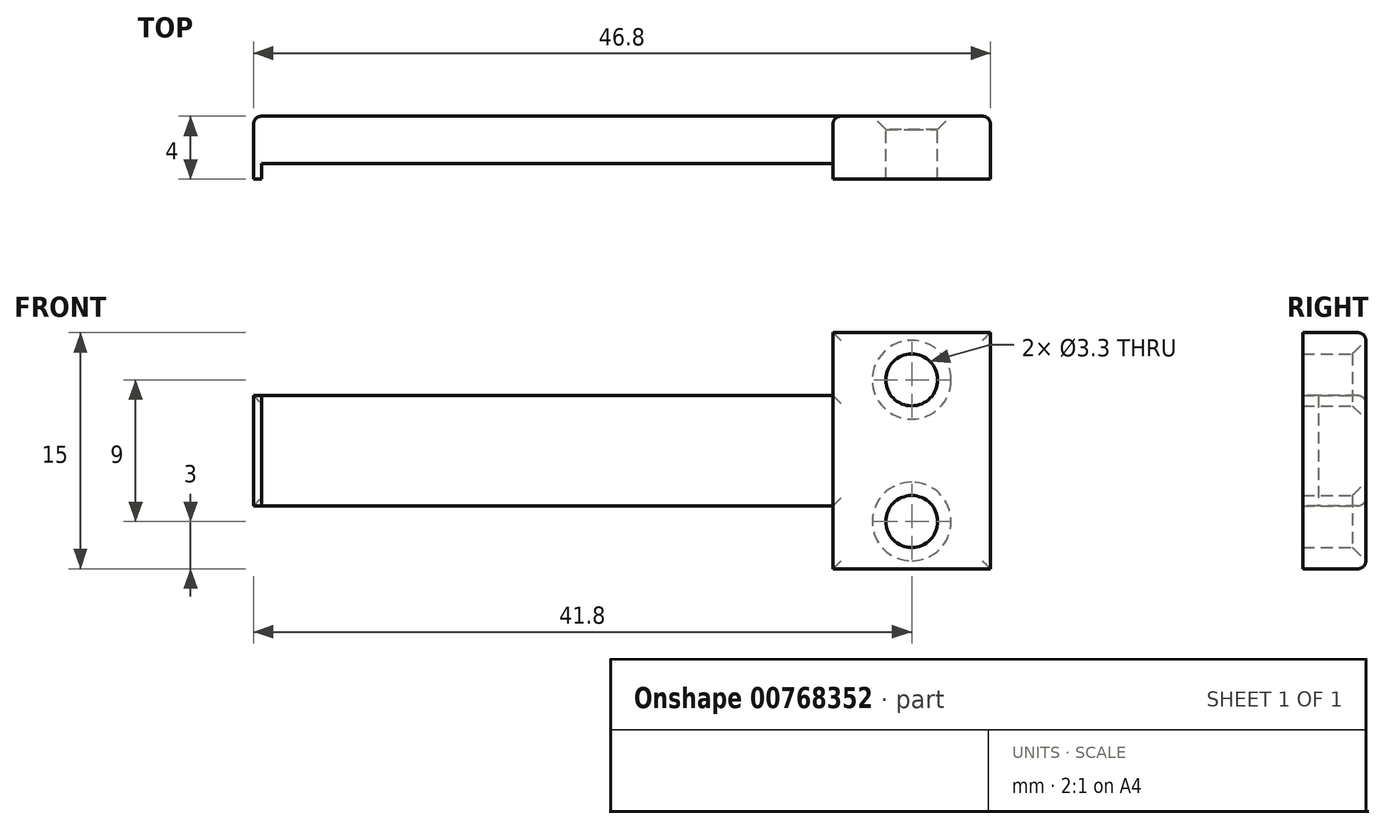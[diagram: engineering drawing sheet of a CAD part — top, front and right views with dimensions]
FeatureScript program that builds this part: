
annotation { "Feature Type Name" : "Feature", "Feature Type Description" : "" }
export const myFeature = defineFeature(function(context is Context, id is Id, definition is map)
    precondition{}
    {
        {
            assignVariable(context, id + "F0", {"name" : "clipwidht", "anyValue" : 7});
        }
        {
            assignVariable(context, id + "F1", {"name" : "footwidht", "anyValue" : 4});
        }
        {
            var Q0;
            Q0=qCreatedBy(makeId("Top.planeOp"),FACE);
            var sketch = newSketch(context, id + "F2", { "sketchPlane" : qUnion([Q0])});
            skLineSegment(sketch, "E0", {"start": v(0, 0) * mm, "end": v(0, 4) * mm});
            skLineSegment(sketch, "E1", {"start": v(0, 4) * mm, "end": v(46.8, 4) * mm});
            skLineSegment(sketch, "E2", {"start": v(46.8, 4) * mm, "end": v(46.8, 0) * mm});
            skLineSegment(sketch, "E3", {"start": v(46.8, 0) * mm, "end": v(36.8, 0) * mm});
            skLineSegment(sketch, "E4", {"start": v(36.8, 0) * mm, "end": v(36.8, 1) * mm});
            skLineSegment(sketch, "E5", {"start": v(36.8, 1) * mm, "end": v(0.5, 1) * mm});
            skLineSegment(sketch, "E6", {"start": v(0.5, 1) * mm, "end": v(0.5, 0) * mm});
            skLineSegment(sketch, "E7", {"start": v(0.5, 0) * mm, "end": v(0, 0) * mm});
            skSolve(sketch);
        }
        {
            var Q0;
            Q0=makeQuery(id+"F2.imprint","IMPRINT",FACE,{"disambiguationData":[TD([[makeQuery(id+"F2.imprint","IMPRINT",EDGE,{"derivedFrom":sQuery(id+"F2.wireOp",EDGE,"E0")}),-1.0]])]});
            extrude(context, id + "F3", {"entities" : qUnion([Q0]), "depth" : (getVariable(context, 'clipwidht')) * mm, "offsetDistance" : 25 * mm});
        }
        {
            var Q0;
            Q0=makeQuery(id+"F3.opExtrude","CAP_FACE",FACE,{"disambiguationData":[OSD([sQuery(id+"F2.wireOp",EDGE,"E0"),sQuery(id+"F2.wireOp",EDGE,"E1"),sQuery(id+"F2.wireOp",EDGE,"E2"),sQuery(id+"F2.wireOp",EDGE,"E3"),sQuery(id+"F2.wireOp",EDGE,"E4"),sQuery(id+"F2.wireOp",EDGE,"E5"),sQuery(id+"F2.wireOp",EDGE,"E6"),sQuery(id+"F2.wireOp",EDGE,"E7")])],"isStart":false});
            var sketch = newSketch(context, id + "F4", { "sketchPlane" : qUnion([Q0])});
            skLineSegment(sketch, "E8.bottom", {"start": v(36.8, 0) * mm, "end": v(46.8, 0) * mm});
            skLineSegment(sketch, "E8.top", {"start": v(36.8, 4) * mm, "end": v(46.8, 4) * mm});
            skLineSegment(sketch, "E8.left", {"start": v(36.8, 0) * mm, "end": v(36.8, 4) * mm});
            skLineSegment(sketch, "E8.right", {"start": v(46.8, 0) * mm, "end": v(46.8, 4) * mm});
            skLineSegment(sketch, "E9", {"start": v(41.8, 4) * mm, "end": v(41.8, 0) * mm, "construction": true});
            skSolve(sketch);
        }
        {
            var Q0;
            {var subQ3=sQuery(id+"F4.wireOp",EDGE,"E8.bottom");Q0=makeQuery(id+"F4.imprint","IMPRINT",FACE,{"disambiguationData":[TD([[makeQuery(id+"F4.imprint","IMPRINT",EDGE,{"derivedFrom":subQ3}),-1.0]])]});}
            extrude(context, id + "F5", {"entities" : qUnion([Q0]), "operationType" : NewBodyOperationType.ADD, "depth" : getVariable(context, 'footwidht') * mm, "offsetDistance" : 25 * mm, "hasSecondDirection" : true, "secondDirectionOppositeDirection" : true, "secondDirectionDepth" : (getVariable(context, 'footwidht') + getVariable(context, 'clipwidht')) * mm});
        }
        {
            var Q0;
            Q0=makeQuery(id+"F5.boolean.opBoolean","MERGE",FACE,{"derivedFrom":[makeQuery(id+"F3.opExtrude","SWEPT_FACE",FACE,{"disambiguationData":[OSD([sQuery(id+"F2.wireOp",EDGE,"E1")])]}),makeQuery(id+"F5.opExtrude","SWEPT_FACE",FACE,{"disambiguationData":[OSD([sQuery(id+"F4.wireOp",EDGE,"E8.top")])]})]});
            var sketch = newSketch(context, id + "F6", { "sketchPlane" : qUnion([Q0])});
            skLineSegment(sketch, "E10", {"start": v(-41.8, 11) * mm, "end": v(-41.8, -4) * mm, "construction": true});
            skLineSegment(sketch, "E11", {"start": v(-36.8, 9) * mm, "end": v(-46.8, 9) * mm, "construction": true});
            skLineSegment(sketch, "E12", {"start": v(-36.8, -2) * mm, "end": v(-46.8, -2) * mm, "construction": true});
            skPoint(sketch, "E13", {"position": v(-41.8, 9) * mm});
            skPoint(sketch, "E14", {"position": v(-41.8, -2) * mm});
            skPoint(sketch, "E15", {"position": v(-41.8, 8) * mm});
            skPoint(sketch, "E16", {"position": v(-41.8, -1) * mm});
            skLineSegment(sketch, "E17", {"start": v(-46.8, 3.5) * mm, "end": v(0, 3.5) * mm, "construction": true});
            skSolve(sketch);
        }
        {
            var Q0;
            Q0=sQuery(id+"F6.wireOp",VERTEX,"E15");
            var Q1;
            Q1=sQuery(id+"F6.wireOp",VERTEX,"E16");
            var Q2;
            Q2=makeQuery(id+"F3.opExtrude","SWEPT_BODY",BODY,{"disambiguationData":[OSD([sQuery(id+"F2.wireOp",EDGE,"E0"),sQuery(id+"F2.wireOp",EDGE,"E1"),sQuery(id+"F2.wireOp",EDGE,"E2"),sQuery(id+"F2.wireOp",EDGE,"E3"),sQuery(id+"F2.wireOp",EDGE,"E4"),sQuery(id+"F2.wireOp",EDGE,"E5"),sQuery(id+"F2.wireOp",EDGE,"E6"),sQuery(id+"F2.wireOp",EDGE,"E7")])]});
            hole(context, id + "F7", {"style" : HoleStyle.C_SINK, "endStyle" : HoleEndStyle.THROUGH, "holeDiameter" : 3.3 * mm, "cSinkDiameter" : 5 * mm, "cSinkAngle" : 90 * degree, "majorDiameter" : 5 * mm, "isTappedThrough" : true, "tappedDepth" : 12 * mm, "tapClearance" : 3, "startFromSketch" : true, "locations" : qUnion([Q0, Q1]), "scope" : qUnion([Q2])});
        }
        {
            var Q0;
            Q0=makeQuery(id+"F3.opExtrude","CAP_EDGE",EDGE,{"disambiguationData":[OSD([sQuery(id+"F2.wireOp",EDGE,"E1")])],"isStart":false});
            var Q1;
            Q1=makeQuery(id+"F3.opExtrude","SWEPT_EDGE",EDGE,{"disambiguationData":[OSD([sQuery(id+"F2.wireOp",EDGE,"E0"),sQuery(id+"F2.wireOp",EDGE,"E1")])]});
            var Q2;
            Q2=makeQuery(id+"F3.opExtrude","CAP_EDGE",EDGE,{"disambiguationData":[OSD([sQuery(id+"F2.wireOp",EDGE,"E1")])],"isStart":true});
            var Q3;
            Q3=makeQuery(id+"F5.opExtrude","CAP_EDGE",EDGE,{"disambiguationData":[OSD([sQuery(id+"F4.wireOp",EDGE,"E8.top")])],"isStart":true});
            var Q4;
            {var subQ0=sQuery(id+"F4.wireOp",EDGE,"E8.left");var subQ1=sQuery(id+"F4.wireOp",EDGE,"E8.top");var subQ2=sQuery(id+"F2.wireOp",EDGE,"E1");Q4=makeQuery(id+"F5.boolean.opBoolean","SPLIT",EDGE,{"disambiguationData":[TD([makeQuery(id+"F5.opExtrude","CAP_FACE",FACE,{"disambiguationData":[OSD([sQuery(id+"F4.wireOp",EDGE,"E8.bottom"),subQ1,subQ0,sQuery(id+"F4.wireOp",EDGE,"E8.right")])],"isStart":true})])],"derivedFrom":makeQuery(id+"F5.opExtrude","SWEPT_EDGE",EDGE,{"disambiguationData":[OSD([subQ2,subQ1,subQ0])]})});}
            var Q5;
            {var subQ0=sQuery(id+"F4.wireOp",EDGE,"E8.left");var subQ1=sQuery(id+"F4.wireOp",EDGE,"E8.top");var subQ2=sQuery(id+"F2.wireOp",EDGE,"E1");Q5=makeQuery(id+"F5.boolean.opBoolean","SPLIT",EDGE,{"disambiguationData":[TD([makeQuery(id+"F5.opExtrude","CAP_FACE",FACE,{"disambiguationData":[OSD([sQuery(id+"F4.wireOp",EDGE,"E8.bottom"),subQ1,subQ0,sQuery(id+"F4.wireOp",EDGE,"E8.right")])],"isStart":false})])],"derivedFrom":makeQuery(id+"F5.opExtrude","SWEPT_EDGE",EDGE,{"disambiguationData":[OSD([subQ2,subQ1,subQ0])]})});}
            var Q6;
            Q6=makeQuery(id+"F5.opExtrude","CAP_EDGE",EDGE,{"disambiguationData":[OSD([sQuery(id+"F4.wireOp",EDGE,"E8.top")])],"isStart":false});
            var Q7;
            Q7=makeQuery(id+"F5.boolean.opBoolean","MERGE",EDGE,{"derivedFrom":[makeQuery(id+"F3.opExtrude","SWEPT_EDGE",EDGE,{"disambiguationData":[OSD([sQuery(id+"F2.wireOp",EDGE,"E1"),sQuery(id+"F2.wireOp",EDGE,"E2")])]}),makeQuery(id+"F5.opExtrude","SWEPT_EDGE",EDGE,{"disambiguationData":[OSD([sQuery(id+"F4.wireOp",EDGE,"E8.top"),sQuery(id+"F4.wireOp",EDGE,"E8.right")])]})]});
            fillet(context, id + "F8", {"entities" : qUnion([Q0, Q1, Q2, Q3, Q4, Q5, Q6, Q7]), "radius" : 0.5 * mm, "tangentPropagation" : true, "allowEdgeOverflow" : false});
        }
    });
